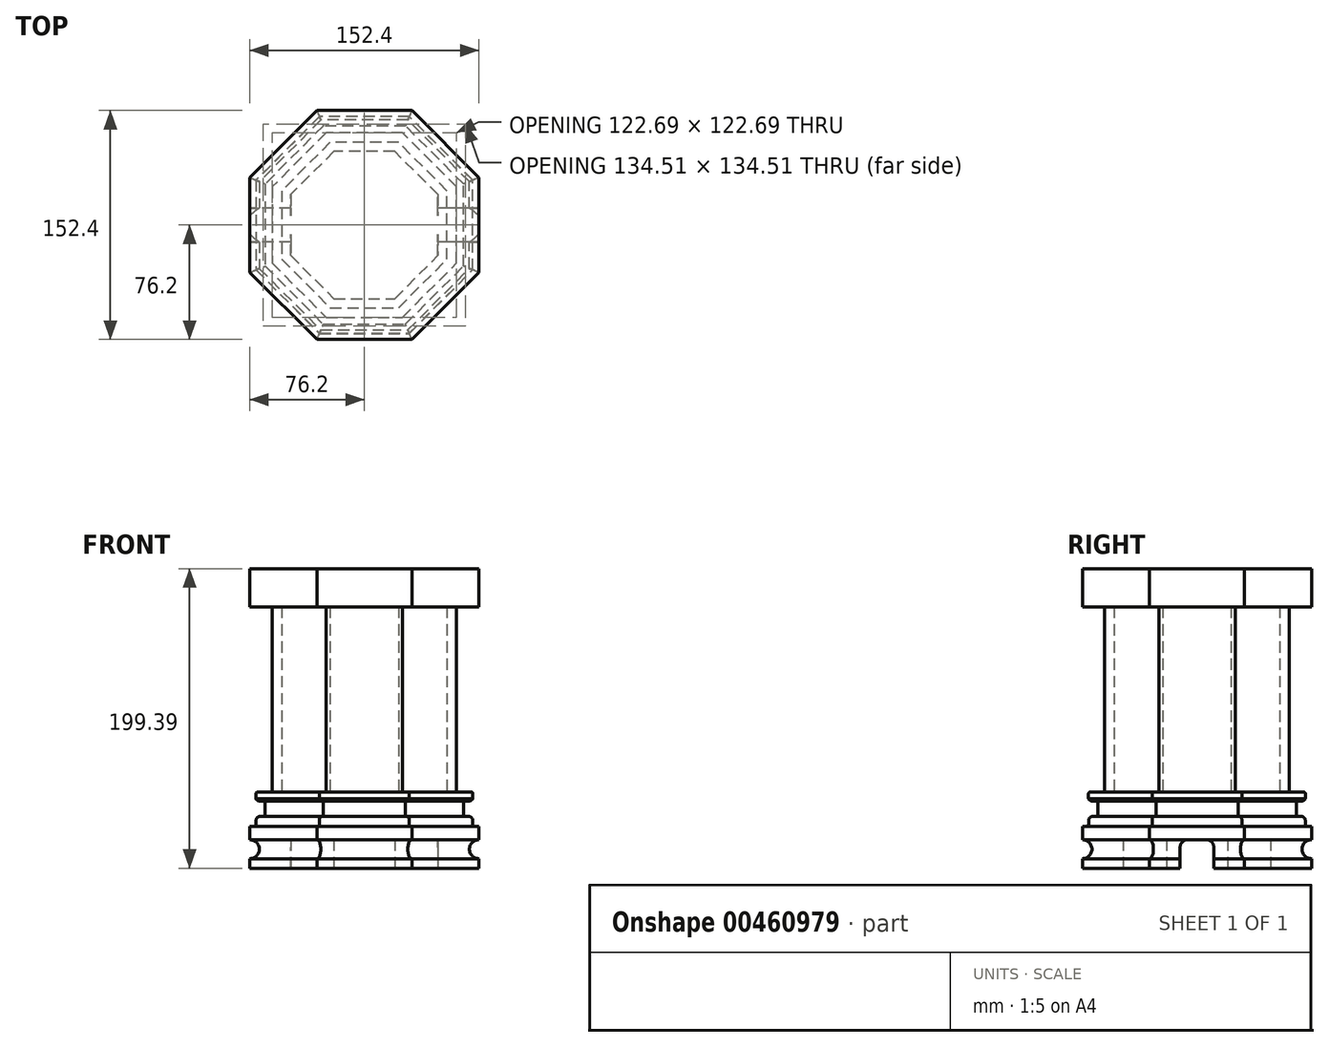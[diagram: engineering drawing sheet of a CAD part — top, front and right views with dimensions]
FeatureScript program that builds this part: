
annotation { "Feature Type Name" : "Feature", "Feature Type Description" : "" }
export const myFeature = defineFeature(function(context is Context, id is Id, definition is map)
    precondition{}
    {
        {
            var Q0;
            Q0=qCreatedBy(makeId("Top.planeOp"),FACE);
            var sketch = newSketch(context, id + "F0", { "sketchPlane" : qUnion([Q0])});
            skCircle(sketch, "E0.cCircle", {"center": v(0, 0) * mm, "radius": 76.2 * mm, "construction": true});
            skLineSegment(sketch, "E0.0", {"start": v(-31.56, 76.2) * mm, "end": v(31.56, 76.2) * mm});
            skLineSegment(sketch, "E0.1", {"start": v(31.56, 76.2) * mm, "end": v(76.2, 31.56) * mm});
            skLineSegment(sketch, "E0.2", {"start": v(76.2, 31.56) * mm, "end": v(76.2, -31.56) * mm});
            skLineSegment(sketch, "E0.3", {"start": v(76.2, -31.56) * mm, "end": v(31.56, -76.2) * mm});
            skLineSegment(sketch, "E0.4", {"start": v(31.56, -76.2) * mm, "end": v(-31.56, -76.2) * mm});
            skLineSegment(sketch, "E0.5", {"start": v(-31.56, -76.2) * mm, "end": v(-76.2, -31.56) * mm});
            skLineSegment(sketch, "E0.6", {"start": v(-76.2, -31.56) * mm, "end": v(-76.2, 31.56) * mm});
            skLineSegment(sketch, "E0.7", {"start": v(-76.2, 31.56) * mm, "end": v(-31.56, 76.2) * mm});
            skPoint(sketch, "E0.0.midPoint", {"position": v(0, 76.2) * mm});
            skSolve(sketch);
        }
        {
            var Q0;
            Q0=makeQuery(id+"F0.imprint","IMPRINT",FACE,{"disambiguationData":[TD([[makeQuery(id+"F0.imprint","IMPRINT",EDGE,{"derivedFrom":sQuery(id+"F0.wireOp",EDGE,"E0.0")}),-1.0]])]});
            extrude(context, id + "F1", {"entities" : qUnion([Q0]), "depth" : 50.8 * mm});
        }
        {
            var Q0;
            Q0=makeQuery(id+"F1.opExtrude","CAP_FACE",FACE,{"disambiguationData":[OSD([sQuery(id+"F0.wireOp",EDGE,"E0.0"),sQuery(id+"F0.wireOp",EDGE,"E0.1"),sQuery(id+"F0.wireOp",EDGE,"E0.2"),sQuery(id+"F0.wireOp",EDGE,"E0.3"),sQuery(id+"F0.wireOp",EDGE,"E0.4"),sQuery(id+"F0.wireOp",EDGE,"E0.5"),sQuery(id+"F0.wireOp",EDGE,"E0.6"),sQuery(id+"F0.wireOp",EDGE,"E0.7")])],"isStart":true});
            var sketch = newSketch(context, id + "F2", { "sketchPlane" : qUnion([Q0])});
            skLineSegment(sketch, "E1.0", {"start": v(31.56, 76.2) * mm, "end": v(-31.56, 76.2) * mm});
            skLineSegment(sketch, "E1.1", {"start": v(-31.56, 76.2) * mm, "end": v(-76.2, 31.56) * mm});
            skLineSegment(sketch, "E1.2", {"start": v(-76.2, 31.56) * mm, "end": v(-76.2, -31.56) * mm});
            skLineSegment(sketch, "E1.3", {"start": v(-76.2, -31.56) * mm, "end": v(-31.56, -76.2) * mm});
            skLineSegment(sketch, "E1.4", {"start": v(-31.56, -76.2) * mm, "end": v(31.56, -76.2) * mm});
            skLineSegment(sketch, "E1.5", {"start": v(76.2, -31.56) * mm, "end": v(76.2, 31.56) * mm});
            skLineSegment(sketch, "E1.6", {"start": v(76.2, 31.56) * mm, "end": v(31.56, 76.2) * mm});
            skLineSegment(sketch, "E1.7", {"start": v(31.56, -76.2) * mm, "end": v(76.2, -31.56) * mm});
            skSolve(sketch);
        }
        {
            var Q0;
            Q0=qCreatedBy(makeId("Right.planeOp"),FACE);
            var sketch = newSketch(context, id + "F3", { "sketchPlane" : qUnion([Q0])});
            skCircle(sketch, "E2", {"center": v(-76.2, 12.7) * mm, "radius": 6.35 * mm});
            skLineSegment(sketch, "E3", {"start": v(-76.2, 12.7) * mm, "end": v(-76.2, 27.99) * mm});
            skLineSegment(sketch, "E4", {"start": v(-76.2, 27.99) * mm, "end": v(-73.32, 27.99) * mm});
            skLineSegment(sketch, "E5", {"start": v(-72.05, 29.26) * mm, "end": v(-72.05, 31.93) * mm});
            skLineSegment(sketch, "E6", {"start": v(-69.5, 34.47) * mm, "end": v(-67.25, 34.47) * mm});
            skLineSegment(sketch, "E7", {"start": v(-65.98, 35.74) * mm, "end": v(-65.98, 43.5) * mm});
            skLineSegment(sketch, "E8", {"start": v(-67.25, 44.77) * mm, "end": v(-69.78, 44.77) * mm});
            skLineSegment(sketch, "E9", {"start": v(-71.68, 45.63) * mm, "end": v(-72.14, 46.16) * mm});
            skLineSegment(sketch, "E10", {"start": v(-72.14, 46.16) * mm, "end": v(-72.14, 49.53) * mm});
            skLineSegment(sketch, "E11", {"start": v(-70.87, 50.8) * mm, "end": v(-67.4, 50.8) * mm});
            skLineSegment(sketch, "E12", {"start": v(-67.4, 50.8) * mm, "end": v(-68.92, 63.26) * mm});
            skLineSegment(sketch, "E13", {"start": v(-68.92, 63.26) * mm, "end": v(-79.7, 63.26) * mm});
            skLineSegment(sketch, "E14", {"start": v(-79.7, 63.26) * mm, "end": v(-76.2, 27.99) * mm});
            skPoint(sketch, "E15.visualSharp", {"position": v(-70.92, 44.77) * mm});
            skArc(sketch, "E15.filletArc", {"start": v(-71.68, 45.63) * mm, "mid": v(-70.82, 45) * mm, "end": v(-69.78, 44.77) * mm});
            skPoint(sketch, "E16.visualSharp", {"position": v(-72.05, 34.47) * mm});
            skArc(sketch, "E16.filletArc", {"start": v(-69.5, 34.47) * mm, "mid": v(-71.3, 33.72) * mm, "end": v(-72.05, 31.93) * mm});
            skPoint(sketch, "E17.visualSharp", {"position": v(-65.98, 44.77) * mm});
            skArc(sketch, "E17.filletArc", {"start": v(-65.98, 43.5) * mm, "mid": v(-66.35, 44.4) * mm, "end": v(-67.25, 44.77) * mm});
            skPoint(sketch, "E18.visualSharp", {"position": v(-65.98, 34.47) * mm});
            skArc(sketch, "E18.filletArc", {"start": v(-67.25, 34.47) * mm, "mid": v(-66.35, 34.84) * mm, "end": v(-65.98, 35.74) * mm});
            skPoint(sketch, "E19.visualSharp", {"position": v(-72.05, 27.99) * mm});
            skArc(sketch, "E19.filletArc", {"start": v(-73.32, 27.99) * mm, "mid": v(-72.42, 28.36) * mm, "end": v(-72.05, 29.26) * mm});
            skPoint(sketch, "E20.visualSharp", {"position": v(-72.14, 50.8) * mm});
            skArc(sketch, "E20.filletArc", {"start": v(-70.87, 50.8) * mm, "mid": v(-71.77, 50.43) * mm, "end": v(-72.14, 49.53) * mm});
            skSolve(sketch);
        }
        {
            var Q0;
            Q0=makeQuery(id+"F3.imprint","IMPRINT",FACE,{"disambiguationData":[TD([[makeQuery(id+"F3.imprint","IMPRINT",EDGE,{"derivedFrom":sQuery(id+"F3.wireOp",EDGE,"E4")}),1.0]])]});
            var Q1;
            Q1=makeQuery(id+"F3.imprint","IMPRINT",FACE,{"disambiguationData":[TD([[makeQuery(id+"F3.imprint","IMPRINT",EDGE,{"derivedFrom":sQuery(id+"F3.wireOp",EDGE,"E2")}),1.0]])]});
            var Q2;
            Q2 = qConstructionFilter(qBodyType(qCreatedBy(id + "F2" ,EDGE), BodyType.WIRE), ConstructionObject.NO);
            sweep(context, id + "F4", {"operationType" : NewBodyOperationType.REMOVE, "profiles" : qUnion([Q0, Q1]), "path" : qUnion([Q2])});
        }
        {
            var Q0;
            Q0=makeQuery(id+"F1.opExtrude","CAP_FACE",FACE,{"disambiguationData":[OSD([sQuery(id+"F0.wireOp",EDGE,"E0.0"),sQuery(id+"F0.wireOp",EDGE,"E0.1"),sQuery(id+"F0.wireOp",EDGE,"E0.2"),sQuery(id+"F0.wireOp",EDGE,"E0.3"),sQuery(id+"F0.wireOp",EDGE,"E0.4"),sQuery(id+"F0.wireOp",EDGE,"E0.5"),sQuery(id+"F0.wireOp",EDGE,"E0.6"),sQuery(id+"F0.wireOp",EDGE,"E0.7")])],"isStart":false});
            var sketch = newSketch(context, id + "F5", { "sketchPlane" : qUnion([Q0])});
            skLineSegment(sketch, "E21.0", {"start": v(61.35, 25.41) * mm, "end": v(25.41, 61.35) * mm});
            skLineSegment(sketch, "E21.1", {"start": v(61.35, -25.41) * mm, "end": v(61.35, 25.41) * mm});
            skLineSegment(sketch, "E21.2", {"start": v(25.41, 61.35) * mm, "end": v(-25.41, 61.35) * mm});
            skLineSegment(sketch, "E21.3", {"start": v(25.41, -61.35) * mm, "end": v(61.35, -25.41) * mm});
            skLineSegment(sketch, "E21.4", {"start": v(-25.41, 61.35) * mm, "end": v(-61.35, 25.41) * mm});
            skLineSegment(sketch, "E21.5", {"start": v(-61.35, 25.41) * mm, "end": v(-61.35, -25.41) * mm});
            skLineSegment(sketch, "E21.6", {"start": v(-61.35, -25.41) * mm, "end": v(-25.41, -61.35) * mm});
            skLineSegment(sketch, "E21.7", {"start": v(-25.41, -61.35) * mm, "end": v(25.41, -61.35) * mm});
            skLineSegment(sketch, "E22.0", {"start": v(-55, -22.78) * mm, "end": v(-22.78, -55) * mm});
            skLineSegment(sketch, "E22.1", {"start": v(-55, 22.78) * mm, "end": v(-55, -22.78) * mm});
            skLineSegment(sketch, "E22.2", {"start": v(-22.78, -55) * mm, "end": v(22.78, -55) * mm});
            skLineSegment(sketch, "E22.3", {"start": v(-22.78, 55) * mm, "end": v(-55, 22.78) * mm});
            skLineSegment(sketch, "E22.4", {"start": v(22.78, -55) * mm, "end": v(55, -22.78) * mm});
            skLineSegment(sketch, "E22.5", {"start": v(55, -22.78) * mm, "end": v(55, 22.78) * mm});
            skLineSegment(sketch, "E22.6", {"start": v(55, 22.78) * mm, "end": v(22.78, 55) * mm});
            skLineSegment(sketch, "E22.7", {"start": v(22.78, 55) * mm, "end": v(-22.78, 55) * mm});
            skSolve(sketch);
        }
        {
            var Q0;
            Q0 = qSketchRegion(id + "F5", true);
            extrude(context, id + "F6", {"entities" : qUnion([Q0]), "operationType" : NewBodyOperationType.ADD, "depth" : 123.19 * mm});
        }
        {
            var Q0;
            Q0=makeQuery(id+"F1.opExtrude","CAP_FACE",FACE,{"disambiguationData":[OSD([sQuery(id+"F0.wireOp",EDGE,"E0.0"),sQuery(id+"F0.wireOp",EDGE,"E0.1"),sQuery(id+"F0.wireOp",EDGE,"E0.2"),sQuery(id+"F0.wireOp",EDGE,"E0.3"),sQuery(id+"F0.wireOp",EDGE,"E0.4"),sQuery(id+"F0.wireOp",EDGE,"E0.5"),sQuery(id+"F0.wireOp",EDGE,"E0.6"),sQuery(id+"F0.wireOp",EDGE,"E0.7")])],"isStart":true});
            var sketch = newSketch(context, id + "F7", { "sketchPlane" : qUnion([Q0])});
            skLineSegment(sketch, "E23.bottom", {"start": v(76.2, -11.18) * mm, "end": v(-76.2, -11.18) * mm});
            skLineSegment(sketch, "E23.top", {"start": v(76.2, 11.18) * mm, "end": v(-76.2, 11.18) * mm});
            skLineSegment(sketch, "E23.left", {"start": v(76.2, -11.18) * mm, "end": v(76.2, 11.18) * mm});
            skLineSegment(sketch, "E23.right", {"start": v(-76.2, -11.18) * mm, "end": v(-76.2, 11.18) * mm});
            skPoint(sketch, "E23.middle", {"position": v(0, 0) * mm});
            skSolve(sketch);
        }
        {
            var Q0;
            Q0 = qSketchRegion(id + "F7", true);
            extrude(context, id + "F8", {"entities" : qUnion([Q0]), "operationType" : NewBodyOperationType.REMOVE, "oppositeDirection" : true, "depth" : 19.05 * mm});
        }
        {
            var Q0;
            Q0=qCreatedBy(makeId("Right.planeOp"),FACE);
            var sketch = newSketch(context, id + "F9", { "sketchPlane" : qUnion([Q0])});
            skLineSegment(sketch, "E24", {"start": v(0, 0) * mm, "end": v(0, 177.7) * mm});
            skSolve(sketch);
        }
        {
            var Q0;
            {var subQ0=sQuery(id+"F0.wireOp",EDGE,"E0.5");var subQ2=sQuery(id+"F0.wireOp",EDGE,"E0.6");var subQ3=makeQuery(id+"F1.opExtrude","SWEPT_FACE",FACE,{"disambiguationData":[OSD([subQ2])]});var subQ5=sQuery(id+"F0.wireOp",EDGE,"E0.4");var subQ6=sQuery(id+"F0.wireOp",EDGE,"E0.3");var subQ7=sQuery(id+"F0.wireOp",EDGE,"E0.2");Q0=makeQuery(id+"FD5fXp806tYpQMa_1.1.F8.boolean.opBoolean","SPLIT",FACE,{"disambiguationData":[TD([subQ3])],"derivedFrom":makeQuery(id+"F8.boolean.opBoolean","SPLIT",FACE,{"disambiguationData":[TD([makeQuery(id+"F1.opExtrude","SWEPT_FACE",FACE,{"disambiguationData":[OSD([subQ6])]})])],"derivedFrom":makeQuery(id+"F1.opExtrude","CAP_FACE",FACE,{"disambiguationData":[OSD([sQuery(id+"F0.wireOp",EDGE,"E0.0"),sQuery(id+"F0.wireOp",EDGE,"E0.1"),subQ7,subQ6,subQ5,subQ0,subQ2,sQuery(id+"F0.wireOp",EDGE,"E0.7")])],"isStart":true})})});}
            var sketch = newSketch(context, id + "F10", { "sketchPlane" : qUnion([Q0])});
            skCircle(sketch, "E25.cCircle", {"center": v(0, 0) * mm, "radius": 48.97 * mm, "construction": true});
            skLineSegment(sketch, "E25.0", {"start": v(-20.29, 48.97) * mm, "end": v(20.29, 48.97) * mm});
            skLineSegment(sketch, "E25.1", {"start": v(20.29, 48.97) * mm, "end": v(48.97, 20.29) * mm});
            skLineSegment(sketch, "E25.2", {"start": v(48.97, 20.29) * mm, "end": v(48.97, -20.29) * mm});
            skLineSegment(sketch, "E25.3", {"start": v(48.97, -20.29) * mm, "end": v(20.29, -48.97) * mm});
            skLineSegment(sketch, "E25.4", {"start": v(20.29, -48.97) * mm, "end": v(-20.29, -48.97) * mm});
            skLineSegment(sketch, "E25.5", {"start": v(-20.29, -48.97) * mm, "end": v(-48.97, -20.29) * mm});
            skLineSegment(sketch, "E25.6", {"start": v(-48.97, -20.29) * mm, "end": v(-48.97, 20.29) * mm});
            skLineSegment(sketch, "E25.7", {"start": v(-48.97, 20.29) * mm, "end": v(-20.29, 48.97) * mm});
            skPoint(sketch, "E25.0.midPoint", {"position": v(0, 48.97) * mm});
            skSolve(sketch);
        }
        {
            var Q0;
            Q0 = qSketchRegion(id + "F10", true);
            var Q1;
            {var subQ0=sQuery(id+"F7.wireOp",EDGE,"E23.right");var subQ1=sQuery(id+"F7.wireOp",EDGE,"E23.left");var subQ2=sQuery(id+"F7.wireOp",EDGE,"E23.top");var subQ3=sQuery(id+"F7.wireOp",EDGE,"E23.bottom");Q1=makeQuery(id+"FD5fXp806tYpQMa_1.3.F8.boolean.opBoolean","MERGE",FACE,{"derivedFrom":[makeQuery(id+"FD5fXp806tYpQMa_1.2.F8.boolean.opBoolean","MERGE",FACE,{"derivedFrom":[makeQuery(id+"FD5fXp806tYpQMa_1.1.F8.boolean.opBoolean","MERGE",FACE,{"derivedFrom":[makeQuery(id+"F8.boolean.opBoolean","COPY",FACE,{"derivedFrom":makeQuery(id+"F8.opExtrude","CAP_FACE",FACE,{"disambiguationData":[OSD([subQ3,subQ2,subQ1,subQ0])],"isStart":false})}),makeQuery(id+"FD5fXp806tYpQMa_1.1.F8.opExtrude","CAP_FACE",FACE,{"disambiguationData":[OSD([subQ3,subQ2,subQ1,subQ0])],"isStart":false})]}),makeQuery(id+"FD5fXp806tYpQMa_1.2.F8.opExtrude","CAP_FACE",FACE,{"disambiguationData":[OSD([subQ3,subQ2,subQ1,subQ0])],"isStart":false})]}),makeQuery(id+"FD5fXp806tYpQMa_1.3.F8.opExtrude","CAP_FACE",FACE,{"disambiguationData":[OSD([subQ3,subQ2,subQ1,subQ0])],"isStart":false})]});}
            extrude(context, id + "F11", {"entities" : qUnion([Q0]), "operationType" : NewBodyOperationType.REMOVE, "endBound" : BoundingType.UP_TO_SURFACE, "oppositeDirection" : true, "endBoundEntityFace" : qUnion([Q1]), "depth" : 25.4 * mm});
        }
        {
            var Q0;
            {var subQ3=sQuery(id+"F7.wireOp",EDGE,"E23.bottom");Q0=makeQuery(id+"FD5fXp806tYpQMa_1.1.F8.boolean.opBoolean","SPLIT",EDGE,{"disambiguationData":[TD([makeQuery(id+"F1.opExtrude","SWEPT_FACE",FACE,{"disambiguationData":[OSD([sQuery(id+"F0.wireOp",EDGE,"E0.6")])]})])],"derivedFrom":makeQuery(id+"F8.boolean.opBoolean","COPY",EDGE,{"derivedFrom":makeQuery(id+"F8.opExtrude","CAP_EDGE",EDGE,{"disambiguationData":[OSD([subQ3])],"isStart":false})})});}
            var Q1;
            {var subQ2=sQuery(id+"F7.wireOp",EDGE,"E23.top");Q1=makeQuery(id+"FD5fXp806tYpQMa_1.1.F8.boolean.opBoolean","SPLIT",EDGE,{"disambiguationData":[TD([makeQuery(id+"F1.opExtrude","SWEPT_FACE",FACE,{"disambiguationData":[OSD([sQuery(id+"F0.wireOp",EDGE,"E0.6")])]})])],"derivedFrom":makeQuery(id+"F8.boolean.opBoolean","COPY",EDGE,{"derivedFrom":makeQuery(id+"F8.opExtrude","CAP_EDGE",EDGE,{"disambiguationData":[OSD([subQ2])],"isStart":false})})});}
            var Q2;
            {var subQ3=sQuery(id+"F7.wireOp",EDGE,"E23.bottom");Q2=makeQuery(id+"FD5fXp806tYpQMa_1.1.F8.boolean.opBoolean","COPY",EDGE,{"disambiguationData":[TD([makeQuery(id+"F1.opExtrude","SWEPT_FACE",FACE,{"disambiguationData":[OSD([sQuery(id+"F0.wireOp",EDGE,"E0.5")])]})])],"derivedFrom":makeQuery(id+"FD5fXp806tYpQMa_1.1.F8.opExtrude","CAP_EDGE",EDGE,{"disambiguationData":[OSD([subQ3])],"isStart":false})});}
            var Q3;
            {var subQ0=sQuery(id+"F7.wireOp",EDGE,"E23.top");Q3=makeQuery(id+"FD5fXp806tYpQMa_1.1.F8.boolean.opBoolean","COPY",EDGE,{"disambiguationData":[TD([makeQuery(id+"F1.opExtrude","SWEPT_FACE",FACE,{"disambiguationData":[OSD([sQuery(id+"F0.wireOp",EDGE,"E0.5")])]})])],"derivedFrom":makeQuery(id+"FD5fXp806tYpQMa_1.1.F8.opExtrude","CAP_EDGE",EDGE,{"disambiguationData":[OSD([subQ0])],"isStart":false})});}
            var Q4;
            {var subQ3=sQuery(id+"F7.wireOp",EDGE,"E23.bottom");var subQ8=sQuery(id+"F0.wireOp",EDGE,"E0.4");Q4=makeQuery(id+"FD5fXp806tYpQMa_1.2.F8.boolean.opBoolean","COPY",EDGE,{"disambiguationData":[TD([makeQuery(id+"F1.opExtrude","SWEPT_FACE",FACE,{"disambiguationData":[OSD([subQ8])]})])],"derivedFrom":makeQuery(id+"FD5fXp806tYpQMa_1.2.F8.opExtrude","CAP_EDGE",EDGE,{"disambiguationData":[OSD([subQ3])],"isStart":false})});}
            var Q5;
            {var subQ2=sQuery(id+"F7.wireOp",EDGE,"E23.top");Q5=makeQuery(id+"FD5fXp806tYpQMa_1.2.F8.boolean.opBoolean","COPY",EDGE,{"disambiguationData":[TD([makeQuery(id+"F1.opExtrude","SWEPT_FACE",FACE,{"disambiguationData":[OSD([sQuery(id+"F0.wireOp",EDGE,"E0.4")])]})])],"derivedFrom":makeQuery(id+"FD5fXp806tYpQMa_1.2.F8.opExtrude","CAP_EDGE",EDGE,{"disambiguationData":[OSD([subQ2])],"isStart":false})});}
            var Q6;
            {var subQ0=sQuery(id+"F7.wireOp",EDGE,"E23.top");Q6=makeQuery(id+"FD5fXp806tYpQMa_1.3.F8.boolean.opBoolean","COPY",EDGE,{"disambiguationData":[TD([makeQuery(id+"F1.opExtrude","SWEPT_FACE",FACE,{"disambiguationData":[OSD([sQuery(id+"F0.wireOp",EDGE,"E0.3")])]})])],"derivedFrom":makeQuery(id+"FD5fXp806tYpQMa_1.3.F8.opExtrude","CAP_EDGE",EDGE,{"disambiguationData":[OSD([subQ0])],"isStart":false})});}
            var Q7;
            {var subQ3=sQuery(id+"F7.wireOp",EDGE,"E23.bottom");var subQ7=sQuery(id+"F0.wireOp",EDGE,"E0.3");Q7=makeQuery(id+"FD5fXp806tYpQMa_1.3.F8.boolean.opBoolean","COPY",EDGE,{"disambiguationData":[TD([makeQuery(id+"F1.opExtrude","SWEPT_FACE",FACE,{"disambiguationData":[OSD([subQ7])]})])],"derivedFrom":makeQuery(id+"FD5fXp806tYpQMa_1.3.F8.opExtrude","CAP_EDGE",EDGE,{"disambiguationData":[OSD([subQ3])],"isStart":false})});}
            var Q8;
            {var subQ0=sQuery(id+"F7.wireOp",EDGE,"E23.top");Q8=makeQuery(id+"FD5fXp806tYpQMa_1.1.F8.boolean.opBoolean","SPLIT",EDGE,{"disambiguationData":[TD([makeQuery(id+"F1.opExtrude","SWEPT_FACE",FACE,{"disambiguationData":[OSD([sQuery(id+"F0.wireOp",EDGE,"E0.2")])]})])],"derivedFrom":makeQuery(id+"F8.boolean.opBoolean","COPY",EDGE,{"derivedFrom":makeQuery(id+"F8.opExtrude","CAP_EDGE",EDGE,{"disambiguationData":[OSD([subQ0])],"isStart":false})})});}
            var Q9;
            {var subQ3=sQuery(id+"F7.wireOp",EDGE,"E23.bottom");Q9=makeQuery(id+"FD5fXp806tYpQMa_1.1.F8.boolean.opBoolean","SPLIT",EDGE,{"disambiguationData":[TD([makeQuery(id+"F1.opExtrude","SWEPT_FACE",FACE,{"disambiguationData":[OSD([sQuery(id+"F0.wireOp",EDGE,"E0.2")])]})])],"derivedFrom":makeQuery(id+"F8.boolean.opBoolean","COPY",EDGE,{"derivedFrom":makeQuery(id+"F8.opExtrude","CAP_EDGE",EDGE,{"disambiguationData":[OSD([subQ3])],"isStart":false})})});}
            var Q10;
            {var subQ2=sQuery(id+"F7.wireOp",EDGE,"E23.top");Q10=makeQuery(id+"FD5fXp806tYpQMa_1.1.F8.boolean.opBoolean","COPY",EDGE,{"disambiguationData":[TD([makeQuery(id+"F1.opExtrude","SWEPT_FACE",FACE,{"disambiguationData":[OSD([sQuery(id+"F0.wireOp",EDGE,"E0.1")])]})])],"derivedFrom":makeQuery(id+"FD5fXp806tYpQMa_1.1.F8.opExtrude","CAP_EDGE",EDGE,{"disambiguationData":[OSD([subQ2])],"isStart":false})});}
            var Q11;
            {var subQ3=sQuery(id+"F7.wireOp",EDGE,"E23.bottom");Q11=makeQuery(id+"FD5fXp806tYpQMa_1.1.F8.boolean.opBoolean","COPY",EDGE,{"disambiguationData":[TD([makeQuery(id+"F1.opExtrude","SWEPT_FACE",FACE,{"disambiguationData":[OSD([sQuery(id+"F0.wireOp",EDGE,"E0.1")])]})])],"derivedFrom":makeQuery(id+"FD5fXp806tYpQMa_1.1.F8.opExtrude","CAP_EDGE",EDGE,{"disambiguationData":[OSD([subQ3])],"isStart":false})});}
            var Q12;
            {var subQ0=sQuery(id+"F7.wireOp",EDGE,"E23.bottom");Q12=makeQuery(id+"FD5fXp806tYpQMa_1.2.F8.boolean.opBoolean","COPY",EDGE,{"disambiguationData":[TD([makeQuery(id+"F1.opExtrude","SWEPT_FACE",FACE,{"disambiguationData":[OSD([sQuery(id+"F0.wireOp",EDGE,"E0.0")])]})])],"derivedFrom":makeQuery(id+"FD5fXp806tYpQMa_1.2.F8.opExtrude","CAP_EDGE",EDGE,{"disambiguationData":[OSD([subQ0])],"isStart":false})});}
            var Q13;
            {var subQ3=sQuery(id+"F7.wireOp",EDGE,"E23.bottom");Q13=makeQuery(id+"FD5fXp806tYpQMa_1.3.F8.boolean.opBoolean","COPY",EDGE,{"disambiguationData":[TD([makeQuery(id+"F1.opExtrude","SWEPT_FACE",FACE,{"disambiguationData":[OSD([sQuery(id+"F0.wireOp",EDGE,"E0.7")])]})])],"derivedFrom":makeQuery(id+"FD5fXp806tYpQMa_1.3.F8.opExtrude","CAP_EDGE",EDGE,{"disambiguationData":[OSD([subQ3])],"isStart":false})});}
            var Q14;
            {var subQ2=sQuery(id+"F7.wireOp",EDGE,"E23.top");var subQ7=sQuery(id+"F0.wireOp",EDGE,"E0.7");Q14=makeQuery(id+"FD5fXp806tYpQMa_1.3.F8.boolean.opBoolean","COPY",EDGE,{"disambiguationData":[TD([makeQuery(id+"F1.opExtrude","SWEPT_FACE",FACE,{"disambiguationData":[OSD([subQ7])]})])],"derivedFrom":makeQuery(id+"FD5fXp806tYpQMa_1.3.F8.opExtrude","CAP_EDGE",EDGE,{"disambiguationData":[OSD([subQ2])],"isStart":false})});}
            var Q15;
            {var subQ2=sQuery(id+"F7.wireOp",EDGE,"E23.top");var subQ5=sQuery(id+"F0.wireOp",EDGE,"E0.0");Q15=makeQuery(id+"FD5fXp806tYpQMa_1.2.F8.boolean.opBoolean","COPY",EDGE,{"disambiguationData":[TD([makeQuery(id+"F1.opExtrude","SWEPT_FACE",FACE,{"disambiguationData":[OSD([subQ5])]})])],"derivedFrom":makeQuery(id+"FD5fXp806tYpQMa_1.2.F8.opExtrude","CAP_EDGE",EDGE,{"disambiguationData":[OSD([subQ2])],"isStart":false})});}
            fillet(context, id + "F12", {"entities" : qUnion([Q0, Q1, Q2, Q3, Q4, Q5, Q6, Q7, Q8, Q9, Q10, Q11, Q12, Q13, Q14, Q15]), "radius" : 5.08 * mm, "tangentPropagation" : true, "allowEdgeOverflow" : false});
        }
        {
            var Q0;
            Q0=makeQuery(id+"F6.opExtrude","CAP_FACE",FACE,{"disambiguationData":[OSD([sQuery(id+"F5.wireOp",EDGE,"E21.0"),sQuery(id+"F5.wireOp",EDGE,"E21.1"),sQuery(id+"F5.wireOp",EDGE,"E21.2"),sQuery(id+"F5.wireOp",EDGE,"E21.3"),sQuery(id+"F5.wireOp",EDGE,"E21.4"),sQuery(id+"F5.wireOp",EDGE,"E21.5"),sQuery(id+"F5.wireOp",EDGE,"E21.6"),sQuery(id+"F5.wireOp",EDGE,"E21.7"),sQuery(id+"F5.wireOp",EDGE,"E22.0"),sQuery(id+"F5.wireOp",EDGE,"E22.1"),sQuery(id+"F5.wireOp",EDGE,"E22.2"),sQuery(id+"F5.wireOp",EDGE,"E22.3"),sQuery(id+"F5.wireOp",EDGE,"E22.4"),sQuery(id+"F5.wireOp",EDGE,"E22.5"),sQuery(id+"F5.wireOp",EDGE,"E22.6"),sQuery(id+"F5.wireOp",EDGE,"E22.7")])],"isStart":false});
            var sketch = newSketch(context, id + "F13", { "sketchPlane" : qUnion([Q0])});
            skLineSegment(sketch, "E26.0", {"start": v(76.2, -31.56) * mm, "end": v(76.2, 31.56) * mm});
            skLineSegment(sketch, "E26.1", {"start": v(31.56, -76.2) * mm, "end": v(76.2, -31.56) * mm});
            skLineSegment(sketch, "E26.2", {"start": v(-31.56, -76.2) * mm, "end": v(31.56, -76.2) * mm});
            skLineSegment(sketch, "E26.3", {"start": v(-76.2, -31.56) * mm, "end": v(-31.56, -76.2) * mm});
            skLineSegment(sketch, "E26.4", {"start": v(-76.2, 31.56) * mm, "end": v(-76.2, -31.56) * mm});
            skLineSegment(sketch, "E26.5", {"start": v(-31.56, 76.2) * mm, "end": v(-76.2, 31.56) * mm});
            skLineSegment(sketch, "E26.6", {"start": v(31.56, 76.2) * mm, "end": v(-31.56, 76.2) * mm});
            skLineSegment(sketch, "E26.7", {"start": v(76.2, 31.56) * mm, "end": v(31.56, 76.2) * mm});
            skSolve(sketch);
        }
        {
            var Q0;
            Q0 = qSketchRegion(id + "F13", true);
            extrude(context, id + "F14", {"entities" : qUnion([Q0]), "operationType" : NewBodyOperationType.ADD, "depth" : 25.4 * mm});
        }
    });
